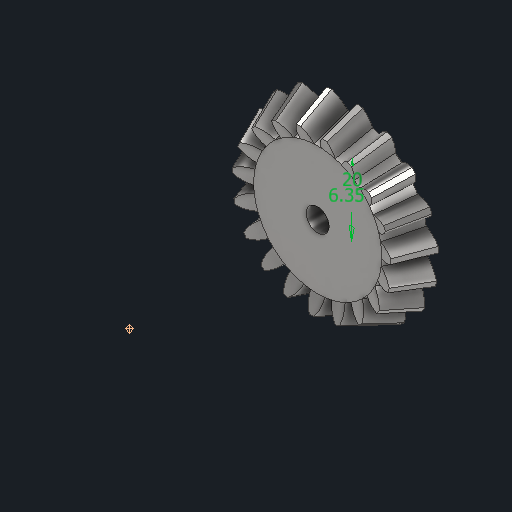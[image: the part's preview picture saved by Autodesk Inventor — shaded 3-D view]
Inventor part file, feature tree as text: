
AUTODESK INVENTOR PART (.ipt)
format: ipt  version: 2022 (Build 260153000, 153)  size: 578,048 bytes
history: native  units: mm
features: other x24, loft x2, pattern_circular x2, sketch x2, extrude x2, chamfer x1
ambient origin geometry x6: Origin, XZ Plane, X Axis, Y Axis, Z Axis, Center Point
bodies: Solid1 (feature_tree)
feature tree (33):
  other  "Top Point"
  other  "Mesh Plane2"
  other  "Teeth Body"
  other  "Start Point"
  other  "Tooth Plane"
  other  "Start Sketch"
  other  "End Point"
  other  "3D Sketch Right"
  other  "End Plane Right"
  loft  "Loft Right"
  pattern_circular  "Circular Pattern Right"  [2 undecoded]
  other  "3D Sketch Left"
  other  "End Plane Left"
  loft  "Loft Left"
  pattern_circular  "Circular Pattern Left"  Angle=90.0deg  [1 undecoded]
  other  "Fix Body"
  sketch  "Sketch8"  dims[d2=52.149033mm d3=10.0mm d4=59.079879mm d5=90.0deg d7=9.577943mm d8=10.649182mm d9=21.38665mm d11=10.275mm d12=8.052853mm d15=8.953519mm d16=17.981267mm d17=0.0mm d18=90.0deg d19=0.0mm d20=90.0deg d21=190.0mm d22=360.0deg d26=428.686656mm d27=9.553763mm d28=47.5mm d29=-3.769093mm d30=8.052853mm d31=8.953519mm d32=17.981267mm d35=0.0mm d37=0.0mm d39=0.0mm d40=90.0deg d41=190.0mm d42=360.0deg d46=90.0deg d47=90.0deg d48=0.0mm d49=0.0mm d50=90.0deg d51=1.65347mm d52=0.0mm d53=0.0mm d54=0.0mm d56=20.48719mm d57=29.692946mm d58=21.882946mm d59=24.964956mm d60=18.398538mm d61=24.964956mm d62=18.398538mm d65=428.686656mm d66=31.5mm d67=47.5mm d68=-3.769093mm d69=9.553763mm d70=8.953519mm d71=17.981267mm d72=8.052853mm d73=18.398538mm d74=24.964956mm d75=0.0mm d77=0.0mm d79=0.0mm d80=90.0deg d81=190.0mm d82=360.0deg d84=10.0mm d85=20.0mm d86=20.0mm d87=10.0mm d88=0.0mm d89=0.0mm d90=90.0deg d91=90.0deg d92=90.0deg d93=90.0deg d94=6.35mm d95=20.0mm d96=5.0mm d97=0.0mm d98=8.0mm d99=0.0mm d100=3.0mm d101=2.0mm d102=45.0deg]
  extrude  "Extrusion1"  Depth=8.0mm
  extrude  "Extrusion2"  Depth=8.0mm
  chamfer  "Chamfer1"  Distance=21.38665mm
  other  "Mesh Plane"
  other  "Top Plane"
  other  "Teeth Body Sketch"
  other  "End Plane"
  other  "End Sketch"
  other  "Helical Curve Left"
  other  "End Sketch Left"
  other  "Body Sketch"
  sketch  "Sketch6"  dims[d0=47.5mm d1=41.92116mm]
  other  "Srf1"
  other  "Helical Curve Right"
  other  "End Sketch Right"
  other  "Pitch Diameter"
note: 3 required parameter values undecoded (feature->parameter linkage not recoverable at this tier; creation-order binding heuristic only, values carry confidence <= 0.55)
